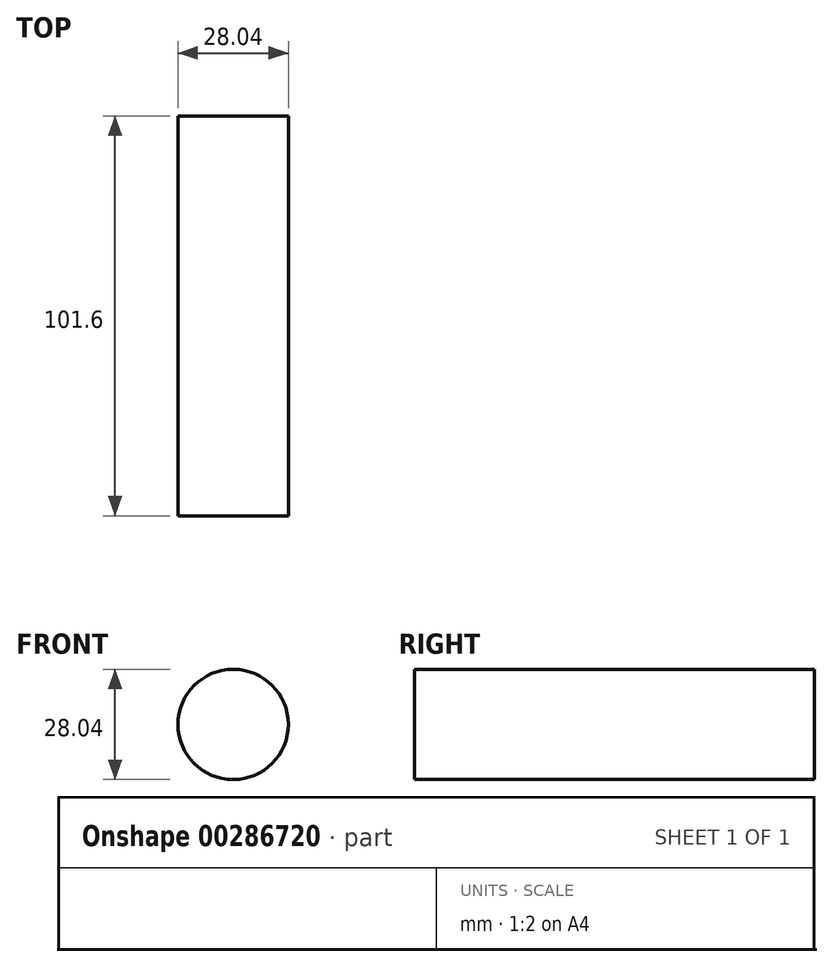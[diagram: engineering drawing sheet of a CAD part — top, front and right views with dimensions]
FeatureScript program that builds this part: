
annotation { "Feature Type Name" : "Feature", "Feature Type Description" : "" }
export const myFeature = defineFeature(function(context is Context, id is Id, definition is map)
    precondition{}
    {
        {
            var Q0;
            Q0=qCreatedBy(makeId("Front.planeOp"),FACE);
            var sketch = newSketch(context, id + "F0", { "sketchPlane" : qUnion([Q0])});
            skCircle(sketch, "E0", {"center": v(21.4, 36.67) * mm, "radius": 14.02 * mm});
            skSolve(sketch);
        }
        {
            var Q0;
            Q0=makeQuery(id+"F0.imprint","IMPRINT",FACE,{"disambiguationData":[TD([[makeQuery(id+"F0.imprint","IMPRINT",EDGE,{"derivedFrom":sQuery(id+"F0.wireOp",EDGE,"E0")}),1.0]])]});
            extrude(context, id + "F1", {"entities" : qUnion([Q0]), "depth" : 101.6 * mm});
        }
    });
